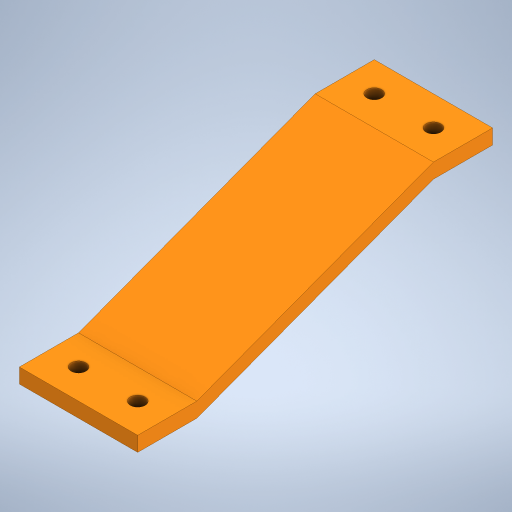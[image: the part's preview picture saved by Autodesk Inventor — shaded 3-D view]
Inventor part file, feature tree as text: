
AUTODESK INVENTOR PART (.ipt)
format: ipt  version: 2023 (Build 270158000, 158)  size: 241,664 bytes
history: native  units: mm
features: extrude x2, sketch x2
ambient origin geometry x8: Origin, YZ Plane, XZ Plane, XY Plane, X Axis, Y Axis, Z Axis, Center Point
bodies: Solid1 (feature_tree)
feature tree (4):
  extrude  "Extrusion1"  Depth=20.0mm
  extrude  "Extrusion2"  Depth=20.0mm
  sketch  "Sketch1"  dims[d0=5.0mm d1=20.0mm]
  sketch  "Sketch2"  dims[d2=5.0mm d3=20.0mm d4=35.0mm d5=120.0mm d6=40.0mm d7=0.0mm d8=5.0mm d9=5.0mm d10=5.0mm d11=5.0mm d12=10.0mm d13=10.0mm d14=10.0mm d15=10.0mm d16=10.0mm d17=10.0mm d18=10.0mm d19=10.0mm d20=90.0mm d21=0.0mm]
